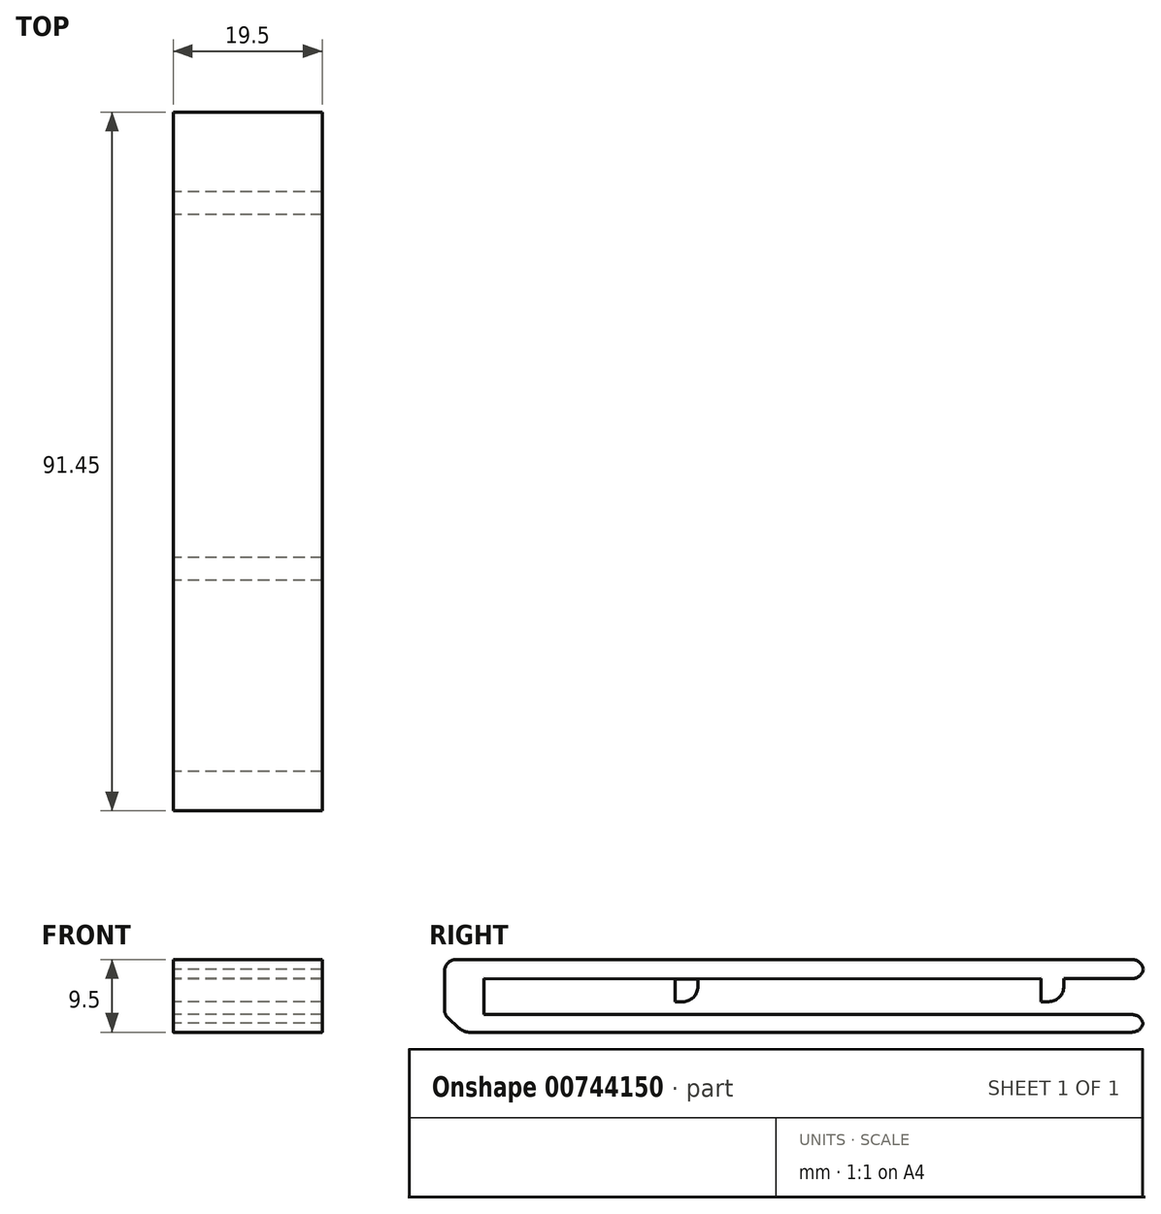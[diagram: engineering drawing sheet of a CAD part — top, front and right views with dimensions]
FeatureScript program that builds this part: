
annotation { "Feature Type Name" : "Feature", "Feature Type Description" : "" }
export const myFeature = defineFeature(function(context is Context, id is Id, definition is map)
    precondition{}
    {
        {
            var Q0;
            Q0=qCreatedBy(makeId("Right.planeOp"),FACE);
            var sketch = newSketch(context, id + "F0", { "sketchPlane" : qUnion([Q0])});
            skLineSegment(sketch, "E0.bottom", {"start": v(-8.01, 1.32) * mm, "end": v(80.99, 1.32) * mm});
            skLineSegment(sketch, "E0.top", {"start": v(-8.01, -0.98) * mm, "end": v(80.99, -0.98) * mm});
            skLineSegment(sketch, "E0.left", {"start": v(-8.01, 1.32) * mm, "end": v(-8.01, -0.98) * mm});
            skLineSegment(sketch, "E0.right", {"start": v(80.99, 1.32) * mm, "end": v(80.99, -0.98) * mm});
            skPoint(sketch, "E1.endSnap0", {"position": v(80.99, 0.17) * mm});
            skLineSegment(sketch, "E2", {"start": v(-8.01, -0.98) * mm, "end": v(-5.32, -0.98) * mm});
            skLineSegment(sketch, "E3", {"start": v(-5.32, -0.98) * mm, "end": v(-5.32, 8.52) * mm});
            skLineSegment(sketch, "E4", {"start": v(-5.32, 8.52) * mm, "end": v(-8.01, 8.52) * mm});
            skLineSegment(sketch, "E5", {"start": v(-8.01, 8.52) * mm, "end": v(-8.01, -0.98) * mm});
            skLineSegment(sketch, "E6", {"start": v(-8.01, 8.52) * mm, "end": v(-8.01, 6.02) * mm});
            skLineSegment(sketch, "E7", {"start": v(-8.01, 6.02) * mm, "end": v(-5.32, 6.02) * mm});
            skLineSegment(sketch, "E8", {"start": v(-5.32, 6.02) * mm, "end": v(-5.32, 8.52) * mm});
            skLineSegment(sketch, "E9", {"start": v(-8.01, 8.52) * mm, "end": v(80.99, 8.52) * mm});
            skLineSegment(sketch, "E10", {"start": v(80.99, 8.52) * mm, "end": v(80.99, 6.02) * mm});
            skLineSegment(sketch, "E11", {"start": v(80.99, 6.02) * mm, "end": v(-5.32, 6.02) * mm});
            skLineSegment(sketch, "E12", {"start": v(-8.01, -0.98) * mm, "end": v(-10.48, 1.32) * mm});
            skLineSegment(sketch, "E13", {"start": v(-10.48, 1.32) * mm, "end": v(-10.48, 6.84) * mm});
            skLineSegment(sketch, "E14", {"start": v(-10.48, 6.84) * mm, "end": v(-10.48, 8.52) * mm});
            skLineSegment(sketch, "E15", {"start": v(-10.48, 8.52) * mm, "end": v(-8.01, 8.52) * mm});
            skLineSegment(sketch, "E16", {"start": v(-5.32, 6.02) * mm, "end": v(-2.32, 6.02) * mm});
            skLineSegment(sketch, "E17", {"start": v(-2.32, 6.02) * mm, "end": v(-2.32, 8.52) * mm});
            skLineSegment(sketch, "E18", {"start": v(11.54, 6) * mm, "end": v(67.57, 6.02) * mm});
            skLineSegment(sketch, "E19.bottom", {"start": v(67.57, 6.02) * mm, "end": v(70.57, 6.02) * mm});
            skLineSegment(sketch, "E19.top", {"start": v(67.57, 3.02) * mm, "end": v(70.57, 3.02) * mm});
            skLineSegment(sketch, "E19.left", {"start": v(67.57, 6.02) * mm, "end": v(67.57, 3.02) * mm});
            skLineSegment(sketch, "E19.right", {"start": v(70.57, 6.02) * mm, "end": v(70.57, 3.02) * mm});
            skLineSegment(sketch, "E20", {"start": v(-8.01, 6.02) * mm, "end": v(-10.48, 6.02) * mm});
            skLineSegment(sketch, "E21", {"start": v(-10.48, 6.02) * mm, "end": v(19.68, 6) * mm});
            skLineSegment(sketch, "E22", {"start": v(19.68, 6) * mm, "end": v(19.68, 8.52) * mm});
            skLineSegment(sketch, "E23.bottom", {"start": v(19.68, 6) * mm, "end": v(22.68, 6) * mm});
            skLineSegment(sketch, "E23.top", {"start": v(19.68, 3) * mm, "end": v(22.68, 3) * mm});
            skLineSegment(sketch, "E23.left", {"start": v(19.68, 6) * mm, "end": v(19.68, 3) * mm});
            skLineSegment(sketch, "E23.right", {"start": v(22.68, 6) * mm, "end": v(22.68, 3) * mm});
            skSolve(sketch);
        }
        {
            var Q0;
            Q0=makeQuery(id+"F0.imprint","IMPRINT",FACE,{"disambiguationData":[TD([[makeQuery(id+"F0.imprint","IMPRINT",EDGE,{"derivedFrom":sQuery(id+"F0.wireOp",EDGE,"E19.top")}),1.0]])]});
            var Q1;
            {var subQ1=sQuery(id+"F0.wireOp",EDGE,"E14");Q1=makeQuery(id+"F0.imprint","IMPRINT",FACE,{"disambiguationData":[TD([[makeQuery(id+"F0.imprint","IMPRINT",EDGE,{"derivedFrom":subQ1}),-1.0]])]});}
            var Q2;
            {var subQ1=sQuery(id+"F0.wireOp",EDGE,"E10");Q2=makeQuery(id+"F0.imprint","IMPRINT",FACE,{"disambiguationData":[TD([[makeQuery(id+"F0.imprint","IMPRINT",EDGE,{"derivedFrom":subQ1}),-1.0]])]});}
            var Q3;
            Q3=makeQuery(id+"F0.imprint","IMPRINT",FACE,{"disambiguationData":[TD([[makeQuery(id+"F0.imprint","IMPRINT",EDGE,{"derivedFrom":sQuery(id+"F0.wireOp",EDGE,"E23.bottom")}),-1.0]])]});
            var Q4;
            {var subQ3=sQuery(id+"F0.wireOp",EDGE,"E0.right");Q4=makeQuery(id+"F0.imprint","IMPRINT",FACE,{"disambiguationData":[TD([[makeQuery(id+"F0.imprint","IMPRINT",EDGE,{"derivedFrom":subQ3}),-1.0]])]});}
            var Q5;
            {var subQ0=sQuery(id+"F0.wireOp",EDGE,"E3");var subQ1=sQuery(id+"F0.wireOp",EDGE,"E0.bottom");var subQ2=makeQuery(id+"F0.imprint","INTERSECT",VERTEX,{"derivedFrom":[subQ1,subQ0]});Q5=makeQuery(id+"F0.imprint","IMPRINT",FACE,{"disambiguationData":[TD([[makeQuery(id+"F0.imprint","IMPRINT",EDGE,{"disambiguationData":[TD([[subQ2,-1.0]])],"derivedFrom":subQ0}),1.0]])]});}
            var Q6;
            {var subQ5=sQuery(id+"F0.wireOp",EDGE,"E0.left");Q6=makeQuery(id+"F0.imprint","IMPRINT",FACE,{"disambiguationData":[TD([[makeQuery(id+"F0.imprint","IMPRINT",EDGE,{"derivedFrom":subQ5}),-1.0]])]});}
            var Q7;
            {var subQ3=sQuery(id+"F0.wireOp",EDGE,"E0.left");Q7=makeQuery(id+"F0.imprint","IMPRINT",FACE,{"disambiguationData":[TD([[makeQuery(id+"F0.imprint","IMPRINT",EDGE,{"derivedFrom":subQ3}),1.0]])]});}
            var Q8;
            {var subQ5=sQuery(id+"F0.wireOp",EDGE,"E17");Q8=makeQuery(id+"F0.imprint","IMPRINT",FACE,{"disambiguationData":[TD([[makeQuery(id+"F0.imprint","IMPRINT",EDGE,{"derivedFrom":subQ5}),1.0]])]});}
            var Q9;
            {var subQ3=sQuery(id+"F0.wireOp",EDGE,"E17");Q9=makeQuery(id+"F0.imprint","IMPRINT",FACE,{"disambiguationData":[TD([[makeQuery(id+"F0.imprint","IMPRINT",EDGE,{"derivedFrom":subQ3}),-1.0]])]});}
            var Q10;
            {var subQ2=sQuery(id+"F0.wireOp",EDGE,"E4");Q10=makeQuery(id+"F0.imprint","IMPRINT",FACE,{"disambiguationData":[TD([[makeQuery(id+"F0.imprint","IMPRINT",EDGE,{"derivedFrom":subQ2}),1.0]])]});}
            var Q11;
            {var subQ1=sQuery(id+"F0.wireOp",EDGE,"E11");var subQ3=sQuery(id+"F0.wireOp",EDGE,"E22");var subQ4=makeQuery(id+"F0.imprint","INTERSECT",VERTEX,{"derivedFrom":[subQ1,subQ3]});Q11=makeQuery(id+"F0.imprint","IMPRINT",FACE,{"disambiguationData":[TD([[makeQuery(id+"F0.imprint","IMPRINT",EDGE,{"disambiguationData":[TD([[subQ4,1.0]])],"derivedFrom":subQ1}),1.0]])]});}
            var Q12;
            {var subQ0=sQuery(id+"F0.wireOp",EDGE,"E7");Q12=makeQuery(id+"F0.imprint","IMPRINT",FACE,{"disambiguationData":[TD([[makeQuery(id+"F0.imprint","IMPRINT",EDGE,{"derivedFrom":subQ0}),-1.0]])]});}
            var Q13;
            {var subQ0=sQuery(id+"F0.wireOp",EDGE,"E11");var subQ3=makeQuery(id+"F0.imprint","INTERSECT",VERTEX,{"derivedFrom":[subQ0,sQuery(id+"F0.wireOp",EDGE,"E17")]});Q13=makeQuery(id+"F0.imprint","IMPRINT",FACE,{"disambiguationData":[TD([[makeQuery(id+"F0.imprint","IMPRINT",EDGE,{"disambiguationData":[TD([[subQ3,1.0]])],"derivedFrom":subQ0}),1.0]])]});}
            var Q14;
            {var subQ3=sQuery(id+"F0.wireOp",EDGE,"E20");Q14=makeQuery(id+"F0.imprint","IMPRINT",FACE,{"disambiguationData":[TD([[makeQuery(id+"F0.imprint","IMPRINT",EDGE,{"derivedFrom":subQ3}),1.0]])]});}
            extrude(context, id + "F1", {"entities" : qUnion([Q0, Q1, Q2, Q3, Q4, Q5, Q6, Q7, Q8, Q9, Q10, Q11, Q12, Q13, Q14]), "depth" : 19.5 * mm, "offsetDistance" : 25 * mm});
        }
        {
            var Q0;
            Q0=makeQuery(id+"F1.opExtrude","SWEPT_EDGE",EDGE,{"disambiguationData":[OSD([sQuery(id+"F0.wireOp",EDGE,"E14"),sQuery(id+"F0.wireOp",EDGE,"E15")])]});
            var Q1;
            Q1=makeQuery(id+"F1.opExtrude","SWEPT_EDGE",EDGE,{"disambiguationData":[OSD([sQuery(id+"F0.wireOp",EDGE,"E9"),sQuery(id+"F0.wireOp",EDGE,"E10")])]});
            var Q2;
            Q2=makeQuery(id+"F1.opExtrude","SWEPT_EDGE",EDGE,{"disambiguationData":[OSD([sQuery(id+"F0.wireOp",EDGE,"E10"),sQuery(id+"F0.wireOp",EDGE,"E11")])]});
            var Q3;
            Q3=makeQuery(id+"F1.opExtrude","SWEPT_EDGE",EDGE,{"disambiguationData":[OSD([sQuery(id+"F0.wireOp",EDGE,"E0.bottom"),sQuery(id+"F0.wireOp",EDGE,"E0.right")])]});
            var Q4;
            Q4=makeQuery(id+"F1.opExtrude","SWEPT_EDGE",EDGE,{"disambiguationData":[OSD([sQuery(id+"F0.wireOp",EDGE,"E12"),sQuery(id+"F0.wireOp",EDGE,"E13")])]});
            var Q5;
            Q5=makeQuery(id+"F1.opExtrude","SWEPT_EDGE",EDGE,{"disambiguationData":[OSD([sQuery(id+"F0.wireOp",EDGE,"E0.top"),sQuery(id+"F0.wireOp",EDGE,"E0.right")])]});
            fillet(context, id + "F2", {"entities" : qUnion([Q0, Q1, Q2, Q3, Q4, Q5]), "radius" : 1.5 * mm, "tangentPropagation" : true, "allowEdgeOverflow" : false});
        }
        {
            var Q0;
            Q0=makeQuery(id+"F1.opExtrude","SWEPT_EDGE",EDGE,{"disambiguationData":[OSD([sQuery(id+"F0.wireOp",EDGE,"E0.top"),sQuery(id+"F0.wireOp",EDGE,"E0.left"),sQuery(id+"F0.wireOp",EDGE,"E12")])]});
            var Q1;
            Q1=makeQuery(id+"F1.opExtrude","SWEPT_EDGE",EDGE,{"disambiguationData":[OSD([sQuery(id+"F0.wireOp",EDGE,"E19.top"),sQuery(id+"F0.wireOp",EDGE,"E19.right")])]});
            var Q2;
            Q2=makeQuery(id+"F1.opExtrude","SWEPT_EDGE",EDGE,{"disambiguationData":[OSD([sQuery(id+"F0.wireOp",EDGE,"E23.top"),sQuery(id+"F0.wireOp",EDGE,"E23.right")])]});
            fillet(context, id + "F3", {"entities" : qUnion([Q0, Q1, Q2]), "radius" : 2 * mm, "tangentPropagation" : true, "allowEdgeOverflow" : false});
        }
    });
